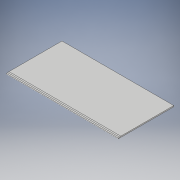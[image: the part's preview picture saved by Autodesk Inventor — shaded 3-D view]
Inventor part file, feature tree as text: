
AUTODESK INVENTOR PART (.ipt)
format: ipt  version: 2017 (Build 210142000, 142)  size: 101,888 bytes
history: native  units: mm
features: fillet x2, extrude x1, sketch x1
ambient origin geometry x8: Origin, YZ Plane, XZ Plane, XY Plane, X Axis, Y Axis, Z Axis, Center Point
bodies: Volumenkörper1 (feature_tree)
feature tree (4):
  extrude  "Extrusion1"  Depth=6.0mm
  fillet  "Rundung1"  Radius=40.0mm
  fillet  "Rundung2"  Radius=10.0mm
  sketch  "Skizze1"  dims[d0=20.0mm d1=1000.0mm d2=40.0mm d3=10.0mm d4=2000.0mm d5=0.0mm d6=100.0mm d7=6.0mm]
